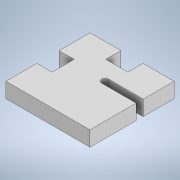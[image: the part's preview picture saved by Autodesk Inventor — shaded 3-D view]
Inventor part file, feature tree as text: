
AUTODESK INVENTOR PART (.ipt)
format: ipt  version: 2020 (Build 240168000, 168)  size: 112,640 bytes
history: native  units: mm
features: extrude x1, sketch x1
ambient origin geometry x8: Origin, YZ Plane, XZ Plane, XY Plane, X Axis, Y Axis, Z Axis, Center Point
bodies: Solide1 (feature_tree)
feature tree (2):
  extrude  "Extrusion1"  Depth=122.0mm
  sketch  "Esquisse1"
